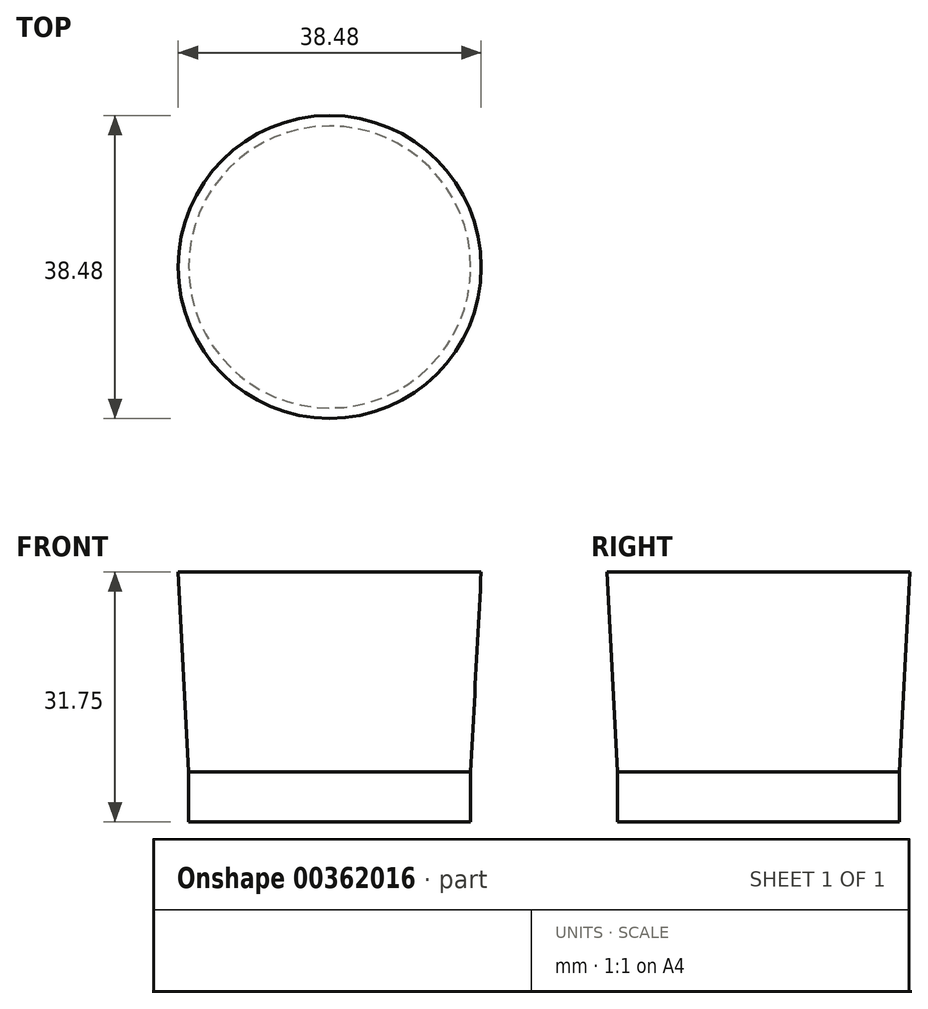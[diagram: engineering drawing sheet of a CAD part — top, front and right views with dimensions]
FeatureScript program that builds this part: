
annotation { "Feature Type Name" : "Feature", "Feature Type Description" : "" }
export const myFeature = defineFeature(function(context is Context, id is Id, definition is map)
    precondition{}
    {
        {
            var Q0;
            Q0=qCreatedBy(makeId("Top.planeOp"),FACE);
            var sketch = newSketch(context, id + "F0", { "sketchPlane" : qUnion([Q0])});
            skCircle(sketch, "E0", {"center": v(0, 0) * mm, "radius": 17.91 * mm});
            skSolve(sketch);
        }
        {
            var Q0;
            Q0=makeQuery(id+"F0.imprint","IMPRINT",FACE,{"disambiguationData":[TD([[makeQuery(id+"F0.imprint","IMPRINT",EDGE,{"derivedFrom":sQuery(id+"F0.wireOp",EDGE,"E0")}),1.0]])]});
            extrude(context, id + "F1", {"entities" : qUnion([Q0]), "depth" : 6.35 * mm});
        }
        {
            var Q0;
            Q0=makeQuery(id+"F1.opExtrude","CAP_FACE",FACE,{"disambiguationData":[OSD([sQuery(id+"F0.wireOp",EDGE,"E0")])],"isStart":false});
            var sketch = newSketch(context, id + "F2", { "sketchPlane" : qUnion([Q0])});
            skSolve(sketch);
        }
        {
            var Q0;
            Q0=makeQuery(id+"F2.imprint","IMPRINT",FACE,{"disambiguationData":[TD([[makeQuery(id+"F2.imprint","IMPRINT",EDGE,{"derivedFrom":makeQuery(id+"F1.opExtrude","CAP_EDGE",EDGE,{"disambiguationData":[OSD([sQuery(id+"F0.wireOp",EDGE,"E0")])],"isStart":false})}),1.0]])]});
            extrude(context, id + "F3", {"entities" : qUnion([Q0]), "operationType" : NewBodyOperationType.ADD, "depth" : 25.4 * mm, "hasDraft" : true, "draftAngle" : 3 * degree});
        }
    });
